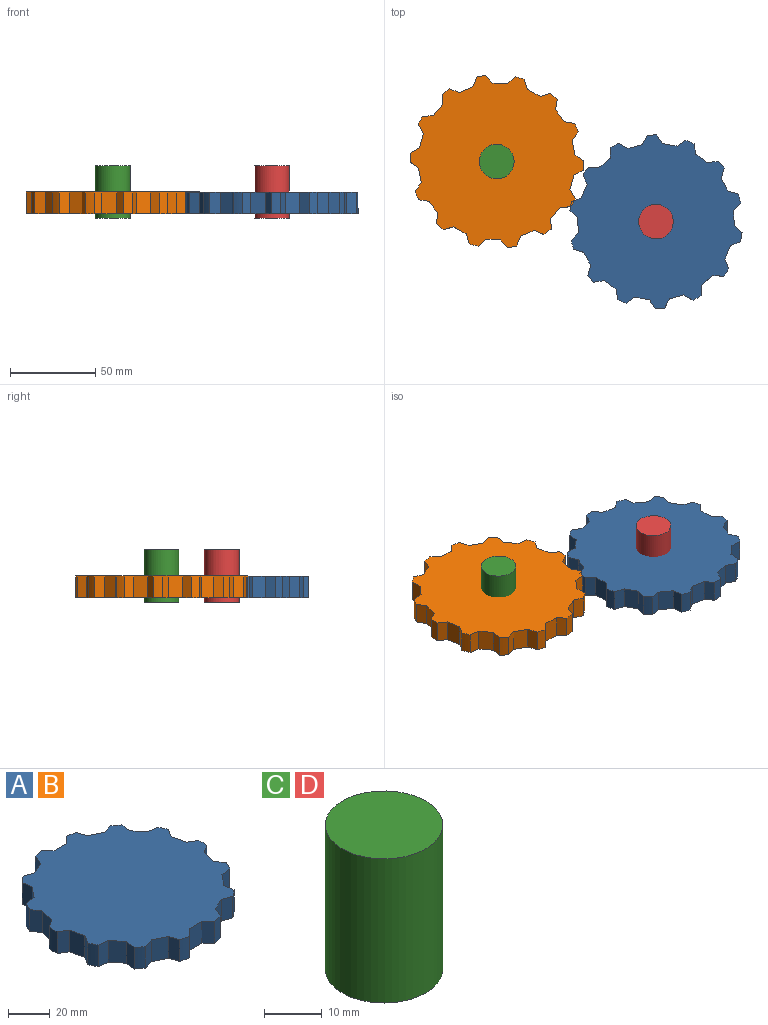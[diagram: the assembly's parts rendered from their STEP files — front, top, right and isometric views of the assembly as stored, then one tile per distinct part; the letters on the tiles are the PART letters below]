
ASSEMBLY  parts=4 mates=2
PART A: 58 faces, bbox 101.6x100.1x12.7 mm
  f0: cylinder r=50.8mm len=12.7mm, axis (0,0,-1), area 68.6mm2, adj f1,f7,f52,f53
  f1: plane 12.7x5.79mm, normal (0.33,0.94,0), area 77.9mm2, adj f0,f2,f52,f53
  f2: plane 12.7x7.78mm, normal (-0.43,0.9,0), area 109.7mm2, adj f1,f3,f52,f53
  f3: plane 12.7x5.79mm, normal (-0.94,0.33,0), area 77.9mm2, adj f2,f52,f53,f54
  f4: cylinder r=50.8mm len=12.7mm, axis (0,0,-1), area 68.6mm2, adj f5,f11,f52,f53
  f5: plane 12.7x6.1mm, normal (-0.11,0.99,0), area 77.9mm2, adj f4,f6,f52,f53
  f6: plane 12.7x6.75mm, normal (-0.78,0.62,0), area 109.7mm2, adj f5,f7,f52,f53
  f7: plane 12.7x6.1mm, normal (-0.99,-0.11,0), area 77.9mm2, adj f0,f6,f52,f53
  f8: cylinder r=50.8mm len=12.7mm, axis (0,0,-1), area 68.6mm2, adj f9,f15,f52,f53
  f9: plane 12.7x5.19mm, normal (-0.53,0.85,0), area 77.9mm2, adj f8,f10,f52,f53
  f10: plane 12.7x8.42mm, normal (-0.97,0.22,0), area 109.7mm2, adj f9,f11,f52,f53
  f11: plane 12.7x5.19mm, normal (-0.85,-0.53,0), area 77.9mm2, adj f4,f10,f52,f53
  f12: cylinder r=50.8mm len=12.7mm, axis (0,0,-1), area 68.6mm2, adj f13,f19,f52,f53
  f13: plane 12.7x5.19mm, normal (-0.85,0.53,0), area 77.9mm2, adj f12,f14,f52,f53
  f14: plane 12.7x8.42mm, normal (-0.97,-0.22,0), area 109.7mm2, adj f13,f15,f52,f53
  f15: plane 12.7x5.19mm, normal (-0.53,-0.85,0), area 77.9mm2, adj f8,f14,f52,f53
  f16: cylinder r=50.8mm len=12.7mm, axis (0,0,-1), area 68.6mm2, adj f17,f23,f52,f53
  f17: plane 12.7x6.1mm, normal (-0.99,0.11,0), area 77.9mm2, adj f16,f18,f52,f53
  f18: plane 12.7x6.75mm, normal (-0.78,-0.62,0), area 109.7mm2, adj f17,f19,f52,f53
  f19: plane 12.7x6.1mm, normal (-0.11,-0.99,0), area 77.9mm2, adj f12,f18,f52,f53
  f20: cylinder r=50.8mm len=12.7mm, axis (0,0,-1), area 68.6mm2, adj f21,f27,f52,f53
  f21: plane 12.7x5.79mm, normal (-0.94,-0.33,0), area 77.9mm2, adj f20,f22,f52,f53
  f22: plane 12.7x7.78mm, normal (-0.43,-0.9,0), area 109.7mm2, adj f21,f23,f52,f53
  f23: plane 12.7x5.79mm, normal (0.33,-0.94,0), area 77.9mm2, adj f16,f22,f52,f53
  f24: cylinder r=50.8mm len=12.7mm, axis (0,0,-1), area 68.6mm2, adj f25,f31,f52,f53
  f25: plane 12.7x4.34mm, normal (-0.71,-0.71,0), area 77.9mm2, adj f24,f26,f52,f53
  f26: plane 12.7x8.64mm, normal (0,-1,0), area 109.7mm2, adj f25,f27,f52,f53
  f27: plane 12.7x4.34mm, normal (0.71,-0.71,0), area 77.9mm2, adj f20,f26,f52,f53
  f28: cylinder r=50.8mm len=12.7mm, axis (0,0,-1), area 68.6mm2, adj f29,f35,f52,f53
  f29: plane 12.7x5.79mm, normal (-0.33,-0.94,0), area 77.9mm2, adj f28,f30,f52,f53
  f30: plane 12.7x7.78mm, normal (0.43,-0.9,0), area 109.7mm2, adj f29,f31,f52,f53
  f31: plane 12.7x5.79mm, normal (0.94,-0.33,0), area 77.9mm2, adj f24,f30,f52,f53
  f32: cylinder r=50.8mm len=12.7mm, axis (0,0,-1), area 68.6mm2, adj f33,f39,f52,f53
  f33: plane 12.7x6.1mm, normal (0.11,-0.99,0), area 77.9mm2, adj f32,f34,f52,f53
  f34: plane 12.7x6.75mm, normal (0.78,-0.62,0), area 109.7mm2, adj f33,f35,f52,f53
  f35: plane 12.7x6.1mm, normal (0.99,0.11,0), area 77.9mm2, adj f28,f34,f52,f53
  f36: cylinder r=50.8mm len=12.7mm, axis (0,0,-1), area 68.6mm2, adj f37,f43,f52,f53
  f37: plane 12.7x5.19mm, normal (0.53,-0.85,0), area 77.9mm2, adj f36,f38,f52,f53
  f38: plane 12.7x8.42mm, normal (0.97,-0.22,0), area 109.7mm2, adj f37,f39,f52,f53
  f39: plane 12.7x5.19mm, normal (0.85,0.53,0), area 77.9mm2, adj f32,f38,f52,f53
  f40: cylinder r=50.8mm len=12.7mm, axis (0,0,-1), area 68.6mm2, adj f41,f47,f52,f53
  f41: plane 12.7x5.19mm, normal (0.85,-0.53,0), area 77.9mm2, adj f40,f42,f52,f53
  f42: plane 12.7x8.42mm, normal (0.97,0.22,0), area 109.7mm2, adj f41,f43,f52,f53
  f43: plane 12.7x5.19mm, normal (0.53,0.85,0), area 77.9mm2, adj f36,f42,f52,f53
  f44: cylinder r=50.8mm len=12.7mm, axis (0,0,-1), area 68.6mm2, adj f45,f51,f52,f53
  f45: plane 12.7x6.1mm, normal (0.99,-0.11,0), area 77.9mm2, adj f44,f46,f52,f53
  f46: plane 12.7x6.75mm, normal (0.78,0.62,0), area 109.7mm2, adj f45,f47,f52,f53
  f47: plane 12.7x6.1mm, normal (0.11,0.99,0), area 77.9mm2, adj f40,f46,f52,f53
  f48: cylinder r=50.8mm len=12.7mm, axis (0,0,-1), area 68.6mm2, adj f49,f52,f53,f57
  f49: plane 12.7x5.79mm, normal (0.94,0.33,0), area 77.9mm2, adj f48,f50,f52,f53
  f50: plane 12.7x7.78mm, normal (0.43,0.9,0), area 109.7mm2, adj f49,f51,f52,f53
  f51: plane 12.7x5.79mm, normal (-0.33,0.94,0), area 77.9mm2, adj f44,f50,f52,f53
  f52: plane 101.6x100.11mm, normal (0,0,1), area 7199.4mm2, adj f0,f1,f2,f3,f4,f5,f6,f7
  f53: plane 101.6x100.11mm, normal (0,0,-1), area 7199.4mm2, adj f0,f1,f2,f3,f4,f5,f6,f7
  f54: cylinder r=50.8mm len=12.7mm, axis (0,0,-1), area 68.6mm2, adj f3,f52,f53,f55
  f55: plane 12.7x4.34mm, normal (0.71,0.71,0), area 77.9mm2, adj f52,f53,f54,f56
  f56: plane 12.7x8.64mm, normal (0,1,0), area 109.7mm2, adj f52,f53,f55,f57
  f57: plane 12.7x4.34mm, normal (-0.71,0.71,0), area 77.9mm2, adj f48,f52,f53,f56
PART B: same geometry as A
PART C: 3 faces, bbox 20.3x20.3x30.5 mm
  f0: cylinder r=10.16mm len=30.48mm, axis (0,0,-1), area 1945.3mm2, adj f1,f2
  f1: plane 20.32x20.32mm, normal (0,0,1), area 324.2mm2, adj f0
  f2: plane 20.32x20.32mm, normal (0,0,-1), area 324.2mm2, adj f0
PART D: same geometry as C
PLACE A rot(axis=(0,0,1),41.2deg) t=(-42.27,-13.15,-12.7)mm
PLACE B rot(axis=(0,0,-1),131.2deg) t=(-135.51,22.05,-12.7)mm
PLACE C t=(-135.51,22.05,-15.24)mm fixed
PLACE D t=(-42.27,-13.15,-15.24)mm fixed
MATE revolute A.f0 <-> D.f0  axis (0,0,1) through (-42.27,-13.15,0)mm
MATE revolute C.f0 <-> B.f0  axis (0,0,-1) through (-135.51,22.05,0)mm
